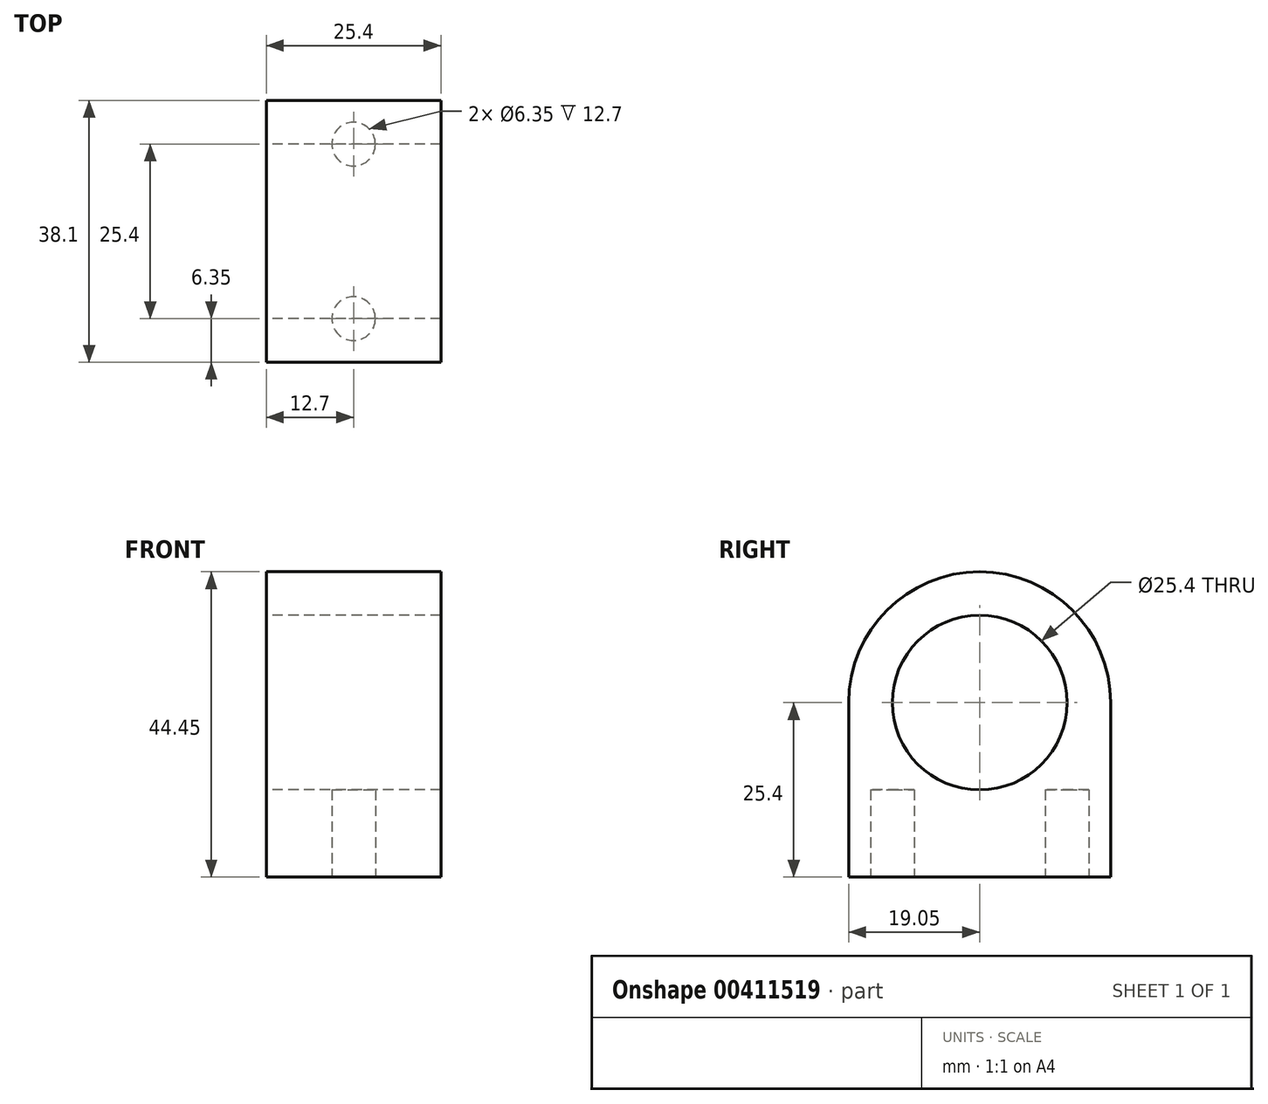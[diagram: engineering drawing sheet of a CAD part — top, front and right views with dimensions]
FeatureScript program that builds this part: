
annotation { "Feature Type Name" : "Feature", "Feature Type Description" : "" }
export const myFeature = defineFeature(function(context is Context, id is Id, definition is map)
    precondition{}
    {
        {
            var Q0;
            Q0=qCreatedBy(makeId("Right.planeOp"),FACE);
            var sketch = newSketch(context, id + "F0", { "sketchPlane" : qUnion([Q0])});
            skCircle(sketch, "E0", {"center": v(0, 0) * mm, "radius": 12.7 * mm});
            skArc(sketch, "E1", {"start": v(19.05, 0) * mm, "mid": v(0, 19.05) * mm, "end": v(-19.05, 0) * mm});
            skLineSegment(sketch, "E2", {"start": v(-19.05, 0) * mm, "end": v(-19.05, -25.4) * mm});
            skLineSegment(sketch, "E3", {"start": v(-19.05, -25.4) * mm, "end": v(19.05, -25.4) * mm});
            skLineSegment(sketch, "E4", {"start": v(19.05, -25.4) * mm, "end": v(19.05, 0) * mm});
            skSolve(sketch);
        }
        {
            var Q0;
            Q0=makeQuery(id+"F0.imprint","IMPRINT",FACE,{"disambiguationData":[TD([[makeQuery(id+"F0.imprint","IMPRINT",EDGE,{"derivedFrom":sQuery(id+"F0.wireOp",EDGE,"E0")}),-1.0]])]});
            extrude(context, id + "F1", {"entities" : qUnion([Q0]), "depth" : 25.4 * mm});
        }
        {
            var Q0;
            Q0=makeQuery(id+"F1.opExtrude","SWEPT_FACE",FACE,{"disambiguationData":[OSD([sQuery(id+"F0.wireOp",EDGE,"E3")])]});
            var sketch = newSketch(context, id + "F2", { "sketchPlane" : qUnion([Q0])});
            skCircle(sketch, "E5", {"center": v(12.7, 12.7) * mm, "radius": 3.17 * mm});
            skCircle(sketch, "E6", {"center": v(12.7, -12.7) * mm, "radius": 3.18 * mm});
            skSolve(sketch);
        }
        {
            var Q0;
            Q0=makeQuery(id+"F2.imprint","IMPRINT",FACE,{"disambiguationData":[TD([[makeQuery(id+"F2.imprint","IMPRINT",EDGE,{"derivedFrom":sQuery(id+"F2.wireOp",EDGE,"E5")}),1.0]])]});
            var Q1;
            Q1=makeQuery(id+"F2.imprint","IMPRINT",FACE,{"disambiguationData":[TD([[makeQuery(id+"F2.imprint","IMPRINT",EDGE,{"derivedFrom":sQuery(id+"F2.wireOp",EDGE,"E6")}),1.0]])]});
            extrude(context, id + "F3", {"entities" : qUnion([Q0, Q1]), "operationType" : NewBodyOperationType.REMOVE, "oppositeDirection" : true, "depth" : 12.7 * mm});
        }
    });
